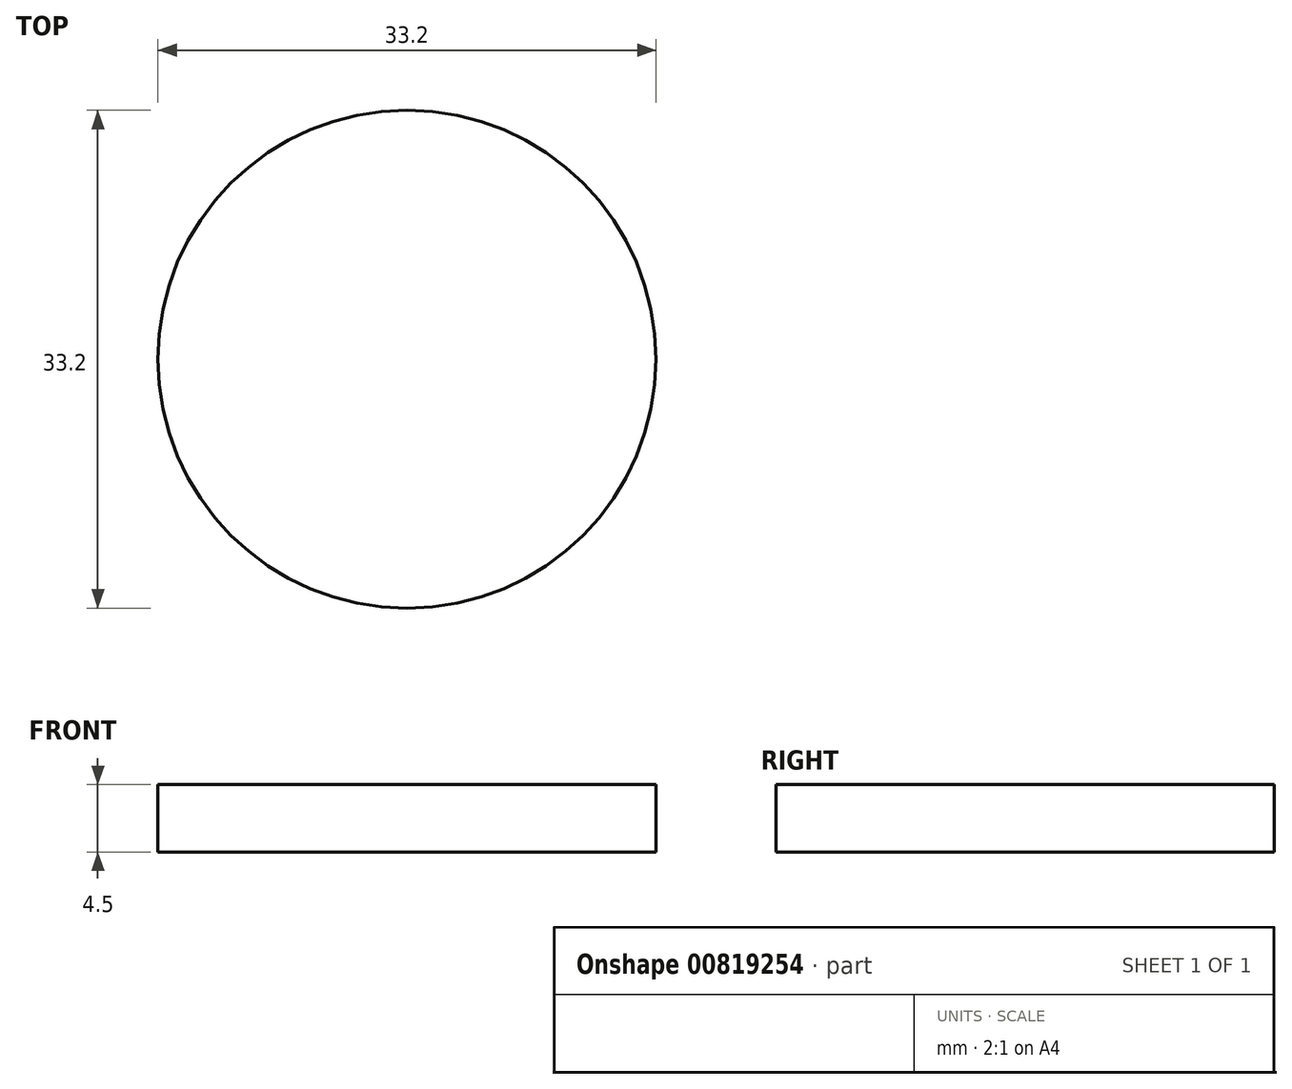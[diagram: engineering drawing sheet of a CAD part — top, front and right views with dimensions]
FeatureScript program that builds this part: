
annotation { "Feature Type Name" : "Feature", "Feature Type Description" : "" }
export const myFeature = defineFeature(function(context is Context, id is Id, definition is map)
    precondition{}
    {
        {
            var Q0;
            Q0=qCreatedBy(makeId("Top.planeOp"),FACE);
            var sketch = newSketch(context, id + "F0", { "sketchPlane" : qUnion([Q0])});
            skCircle(sketch, "E0", {"center": v(0, 0) * mm, "radius": 16.6 * mm});
            skSolve(sketch);
        }
        {
            var Q0;
            Q0=makeQuery(id+"F0.imprint","IMPRINT",FACE,{"disambiguationData":[TD([[makeQuery(id+"F0.imprint","IMPRINT",EDGE,{"derivedFrom":sQuery(id+"F0.wireOp",EDGE,"E0")}),1.0]])]});
            extrude(context, id + "F1", {"entities" : qUnion([Q0]), "depth" : 4.5 * mm, "offsetDistance" : 25.4 * mm});
        }
    });
